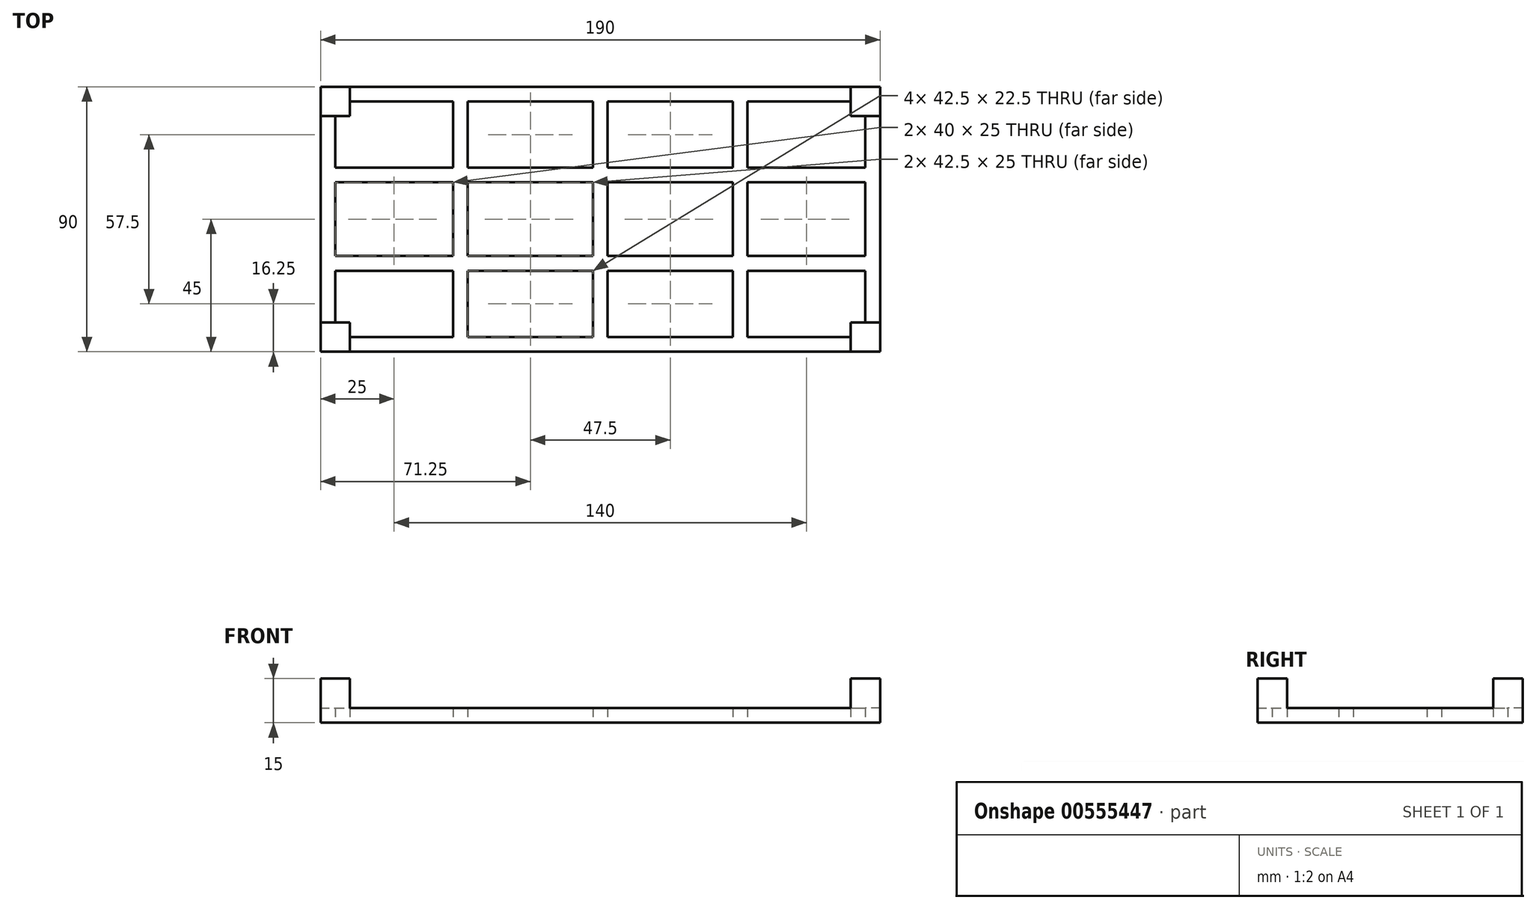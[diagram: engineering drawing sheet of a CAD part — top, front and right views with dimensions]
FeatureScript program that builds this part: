
annotation { "Feature Type Name" : "Feature", "Feature Type Description" : "" }
export const myFeature = defineFeature(function(context is Context, id is Id, definition is map)
    precondition{}
    {
        {
            var Q0;
            Q0=qCreatedBy(makeId("Top.planeOp"),FACE);
            var sketch = newSketch(context, id + "F0", { "sketchPlane" : qUnion([Q0])});
            skLineSegment(sketch, "E0.bottom", {"start": v(0, 0) * mm, "end": v(190, 0) * mm});
            skLineSegment(sketch, "E0.top", {"start": v(0, 90) * mm, "end": v(190, 90) * mm});
            skLineSegment(sketch, "E0.left", {"start": v(0, 0) * mm, "end": v(0, 90) * mm});
            skLineSegment(sketch, "E0.right", {"start": v(190, 0) * mm, "end": v(190, 90) * mm});
            skLineSegment(sketch, "E1", {"start": v(-5.2, 60) * mm, "end": v(194.64, 60) * mm, "construction": true});
            skLineSegment(sketch, "E2", {"start": v(-4.31, 30) * mm, "end": v(194.29, 30) * mm, "construction": true});
            skLineSegment(sketch, "E3", {"start": v(47.5, 94.98) * mm, "end": v(47.5, -5.37) * mm, "construction": true});
            skLineSegment(sketch, "E4", {"start": v(95, 95.69) * mm, "end": v(95, -7.31) * mm, "construction": true});
            skLineSegment(sketch, "E5", {"start": v(142.5, 96.04) * mm, "end": v(142.5, -7.5) * mm, "construction": true});
            skLineSegment(sketch, "E6", {"start": v(45, 85) * mm, "end": v(45, 62.5) * mm});
            skLineSegment(sketch, "E7", {"start": v(92.5, 85) * mm, "end": v(92.5, 62.5) * mm});
            skLineSegment(sketch, "E8", {"start": v(5, 62.5) * mm, "end": v(45, 62.5) * mm});
            skLineSegment(sketch, "E9", {"start": v(5, 57.5) * mm, "end": v(45, 57.5) * mm});
            skLineSegment(sketch, "E10", {"start": v(0, 80) * mm, "end": v(10, 80) * mm});
            skLineSegment(sketch, "E11", {"start": v(10, 90) * mm, "end": v(10, 80) * mm});
            skLineSegment(sketch, "E12", {"start": v(10, 0) * mm, "end": v(10, 10) * mm});
            skLineSegment(sketch, "E13", {"start": v(10, 10) * mm, "end": v(0, 10) * mm});
            skLineSegment(sketch, "E14", {"start": v(190, 10) * mm, "end": v(180, 10) * mm});
            skLineSegment(sketch, "E15", {"start": v(180, 10) * mm, "end": v(180, 0) * mm});
            skLineSegment(sketch, "E16", {"start": v(190, 80) * mm, "end": v(180, 80) * mm});
            skLineSegment(sketch, "E17", {"start": v(180, 80) * mm, "end": v(180, 90) * mm});
            skLineSegment(sketch, "E18.trimOffspring", {"start": v(50, 85) * mm, "end": v(92.5, 85) * mm});
            skLineSegment(sketch, "E19.trimOffspring", {"start": v(10, 85) * mm, "end": v(45, 85) * mm});
            skLineSegment(sketch, "E20.trimOffspring", {"start": v(50, 62.5) * mm, "end": v(92.5, 62.5) * mm});
            skLineSegment(sketch, "E21.trimOffspring", {"start": v(50, 62.5) * mm, "end": v(50, 85) * mm});
            skLineSegment(sketch, "E22.trimOffspring", {"start": v(50, 57.5) * mm, "end": v(92.5, 57.5) * mm});
            skLineSegment(sketch, "E23.trimOffspring", {"start": v(45, 57.5) * mm, "end": v(45, 32.5) * mm});
            skLineSegment(sketch, "E24.trimOffspring", {"start": v(5, 62.5) * mm, "end": v(5, 80) * mm});
            skLineSegment(sketch, "E25.trimOffspring", {"start": v(5, 32.5) * mm, "end": v(5, 57.5) * mm});
            skLineSegment(sketch, "E26.trimOffspring", {"start": v(5, 27.5) * mm, "end": v(45, 27.5) * mm});
            skLineSegment(sketch, "E27.trimOffspring", {"start": v(5, 32.5) * mm, "end": v(45, 32.5) * mm});
            skLineSegment(sketch, "E28.trimOffspring", {"start": v(5, 10) * mm, "end": v(5, 27.5) * mm});
            skLineSegment(sketch, "E29.trimOffspring", {"start": v(10, 5) * mm, "end": v(45, 5) * mm});
            skLineSegment(sketch, "E30.trimOffspring", {"start": v(50, 32.5) * mm, "end": v(92.5, 32.5) * mm});
            skLineSegment(sketch, "E31.trimOffspring", {"start": v(50, 32.5) * mm, "end": v(50, 57.5) * mm});
            skLineSegment(sketch, "E32.trimOffspring", {"start": v(50, 27.5) * mm, "end": v(92.5, 27.5) * mm});
            skLineSegment(sketch, "E33.trimOffspring", {"start": v(45, 27.5) * mm, "end": v(45, 5) * mm});
            skLineSegment(sketch, "E34.trimOffspring", {"start": v(92.5, 27.5) * mm, "end": v(92.5, 5) * mm});
            skLineSegment(sketch, "E35.trimOffspring", {"start": v(97.5, 27.5) * mm, "end": v(140, 27.5) * mm});
            skLineSegment(sketch, "E36.trimOffspring", {"start": v(97.5, 32.5) * mm, "end": v(97.5, 57.5) * mm});
            skLineSegment(sketch, "E37.trimOffspring", {"start": v(97.5, 32.5) * mm, "end": v(140, 32.5) * mm});
            skLineSegment(sketch, "E38.trimOffspring", {"start": v(97.5, 57.5) * mm, "end": v(140, 57.5) * mm});
            skLineSegment(sketch, "E39.trimOffspring", {"start": v(97.5, 62.5) * mm, "end": v(97.5, 85) * mm});
            skLineSegment(sketch, "E40.trimOffspring", {"start": v(97.5, 62.5) * mm, "end": v(140, 62.5) * mm});
            skLineSegment(sketch, "E41.trimOffspring", {"start": v(92.5, 57.5) * mm, "end": v(92.5, 32.5) * mm});
            skLineSegment(sketch, "E42.trimOffspring", {"start": v(50, 5) * mm, "end": v(92.5, 5) * mm});
            skLineSegment(sketch, "E43.trimOffspring", {"start": v(50, 5) * mm, "end": v(50, 27.5) * mm});
            skLineSegment(sketch, "E44.trimOffspring", {"start": v(97.5, 5) * mm, "end": v(140, 5) * mm});
            skLineSegment(sketch, "E45.trimOffspring", {"start": v(97.5, 5) * mm, "end": v(97.5, 27.5) * mm});
            skLineSegment(sketch, "E46.trimOffspring", {"start": v(97.5, 85) * mm, "end": v(140, 85) * mm});
            skLineSegment(sketch, "E47.trimOffspring", {"start": v(140, 85) * mm, "end": v(140, 62.5) * mm});
            skLineSegment(sketch, "E48.trimOffspring", {"start": v(145, 85) * mm, "end": v(180, 85) * mm});
            skLineSegment(sketch, "E49.trimOffspring", {"start": v(145, 62.5) * mm, "end": v(185, 62.5) * mm});
            skLineSegment(sketch, "E50.trimOffspring", {"start": v(140, 57.5) * mm, "end": v(140, 32.5) * mm});
            skLineSegment(sketch, "E51.trimOffspring", {"start": v(145, 57.5) * mm, "end": v(185, 57.5) * mm});
            skLineSegment(sketch, "E52.trimOffspring", {"start": v(145, 62.5) * mm, "end": v(145, 85) * mm});
            skLineSegment(sketch, "E53.trimOffspring", {"start": v(145, 32.5) * mm, "end": v(185, 32.5) * mm});
            skLineSegment(sketch, "E54.trimOffspring", {"start": v(145, 27.5) * mm, "end": v(185, 27.5) * mm});
            skLineSegment(sketch, "E55.trimOffspring", {"start": v(145, 32.5) * mm, "end": v(145, 57.5) * mm});
            skLineSegment(sketch, "E56.trimOffspring", {"start": v(140, 27.5) * mm, "end": v(140, 5) * mm});
            skLineSegment(sketch, "E57.trimOffspring", {"start": v(145, 5) * mm, "end": v(180, 5) * mm});
            skLineSegment(sketch, "E58.trimOffspring", {"start": v(145, 5) * mm, "end": v(145, 27.5) * mm});
            skLineSegment(sketch, "E59.trimOffspring", {"start": v(185, 10) * mm, "end": v(185, 27.5) * mm});
            skLineSegment(sketch, "E60.trimOffspring", {"start": v(185, 32.5) * mm, "end": v(185, 57.5) * mm});
            skLineSegment(sketch, "E61.trimOffspring", {"start": v(185, 62.5) * mm, "end": v(185, 80) * mm});
            skSolve(sketch);
        }
        {
            var Q0;
            Q0=makeQuery(id+"F0.imprint","IMPRINT",FACE,{"disambiguationData":[TD([[makeQuery(id+"F0.imprint","IMPRINT",EDGE,{"derivedFrom":sQuery(id+"F0.wireOp",EDGE,"E6")}),1.0]])]});
            var Q1;
            {var subQ4=sQuery(id+"F0.wireOp",EDGE,"E0.left");var subQ6=sQuery(id+"F0.wireOp",EDGE,"E0.top");var subQ7=makeQuery(id+"F0.imprint","INTERSECT",VERTEX,{"derivedFrom":[subQ6,subQ4]});Q1=makeQuery(id+"F0.imprint","IMPRINT",FACE,{"disambiguationData":[TD([[makeQuery(id+"F0.imprint","IMPRINT",EDGE,{"disambiguationData":[TD([[subQ7,-1.0]])],"derivedFrom":subQ6}),-1.0]])]});}
            var Q2;
            {var subQ4=sQuery(id+"F0.wireOp",EDGE,"E0.left");var subQ5=sQuery(id+"F0.wireOp",EDGE,"E0.bottom");var subQ6=makeQuery(id+"F0.imprint","INTERSECT",VERTEX,{"derivedFrom":[subQ5,subQ4]});Q2=makeQuery(id+"F0.imprint","IMPRINT",FACE,{"disambiguationData":[TD([[makeQuery(id+"F0.imprint","IMPRINT",EDGE,{"disambiguationData":[TD([[subQ6,-1.0]])],"derivedFrom":subQ5}),1.0]])]});}
            var Q3;
            {var subQ4=sQuery(id+"F0.wireOp",EDGE,"E0.right");var subQ6=sQuery(id+"F0.wireOp",EDGE,"E0.top");var subQ7=makeQuery(id+"F0.imprint","INTERSECT",VERTEX,{"derivedFrom":[subQ6,subQ4]});Q3=makeQuery(id+"F0.imprint","IMPRINT",FACE,{"disambiguationData":[TD([[makeQuery(id+"F0.imprint","IMPRINT",EDGE,{"disambiguationData":[TD([[subQ7,1.0]])],"derivedFrom":subQ6}),-1.0]])]});}
            var Q4;
            {var subQ4=sQuery(id+"F0.wireOp",EDGE,"E0.right");var subQ6=sQuery(id+"F0.wireOp",EDGE,"E0.bottom");var subQ7=makeQuery(id+"F0.imprint","INTERSECT",VERTEX,{"derivedFrom":[subQ6,subQ4]});Q4=makeQuery(id+"F0.imprint","IMPRINT",FACE,{"disambiguationData":[TD([[makeQuery(id+"F0.imprint","IMPRINT",EDGE,{"disambiguationData":[TD([[subQ7,1.0]])],"derivedFrom":subQ6}),1.0]])]});}
            extrude(context, id + "F1", {"entities" : qUnion([Q0, Q1, Q2, Q3, Q4]), "depth" : 5 * mm, "offsetDistance" : 25 * mm});
        }
        {
            var Q0;
            Q0=makeQuery(id+"F1.opExtrude","CAP_FACE",FACE,{"disambiguationData":[OSD([sQuery(id+"F0.wireOp",EDGE,"E0.bottom"),sQuery(id+"F0.wireOp",EDGE,"E0.top"),sQuery(id+"F0.wireOp",EDGE,"E0.left"),sQuery(id+"F0.wireOp",EDGE,"E0.right"),sQuery(id+"F0.wireOp",EDGE,"E6"),sQuery(id+"F0.wireOp",EDGE,"E7"),sQuery(id+"F0.wireOp",EDGE,"E8"),sQuery(id+"F0.wireOp",EDGE,"E9"),sQuery(id+"F0.wireOp",EDGE,"E10"),sQuery(id+"F0.wireOp",EDGE,"E11"),sQuery(id+"F0.wireOp",EDGE,"E12"),sQuery(id+"F0.wireOp",EDGE,"E13"),sQuery(id+"F0.wireOp",EDGE,"E14"),sQuery(id+"F0.wireOp",EDGE,"E15"),sQuery(id+"F0.wireOp",EDGE,"E16"),sQuery(id+"F0.wireOp",EDGE,"E17"),sQuery(id+"F0.wireOp",EDGE,"E18.trimOffspring"),sQuery(id+"F0.wireOp",EDGE,"E19.trimOffspring"),sQuery(id+"F0.wireOp",EDGE,"E20.trimOffspring"),sQuery(id+"F0.wireOp",EDGE,"E21.trimOffspring"),sQuery(id+"F0.wireOp",EDGE,"E22.trimOffspring"),sQuery(id+"F0.wireOp",EDGE,"E23.trimOffspring"),sQuery(id+"F0.wireOp",EDGE,"E24.trimOffspring"),sQuery(id+"F0.wireOp",EDGE,"E25.trimOffspring"),sQuery(id+"F0.wireOp",EDGE,"E26.trimOffspring"),sQuery(id+"F0.wireOp",EDGE,"E27.trimOffspring"),sQuery(id+"F0.wireOp",EDGE,"E28.trimOffspring"),sQuery(id+"F0.wireOp",EDGE,"E29.trimOffspring"),sQuery(id+"F0.wireOp",EDGE,"E30.trimOffspring"),sQuery(id+"F0.wireOp",EDGE,"E31.trimOffspring"),sQuery(id+"F0.wireOp",EDGE,"E32.trimOffspring"),sQuery(id+"F0.wireOp",EDGE,"E33.trimOffspring"),sQuery(id+"F0.wireOp",EDGE,"E34.trimOffspring"),sQuery(id+"F0.wireOp",EDGE,"E35.trimOffspring"),sQuery(id+"F0.wireOp",EDGE,"E36.trimOffspring"),sQuery(id+"F0.wireOp",EDGE,"E37.trimOffspring"),sQuery(id+"F0.wireOp",EDGE,"E38.trimOffspring"),sQuery(id+"F0.wireOp",EDGE,"E39.trimOffspring"),sQuery(id+"F0.wireOp",EDGE,"E40.trimOffspring"),sQuery(id+"F0.wireOp",EDGE,"E41.trimOffspring"),sQuery(id+"F0.wireOp",EDGE,"E42.trimOffspring"),sQuery(id+"F0.wireOp",EDGE,"E43.trimOffspring"),sQuery(id+"F0.wireOp",EDGE,"E44.trimOffspring"),sQuery(id+"F0.wireOp",EDGE,"E45.trimOffspring"),sQuery(id+"F0.wireOp",EDGE,"E46.trimOffspring"),sQuery(id+"F0.wireOp",EDGE,"E47.trimOffspring"),sQuery(id+"F0.wireOp",EDGE,"E48.trimOffspring"),sQuery(id+"F0.wireOp",EDGE,"E49.trimOffspring"),sQuery(id+"F0.wireOp",EDGE,"E50.trimOffspring"),sQuery(id+"F0.wireOp",EDGE,"E51.trimOffspring"),sQuery(id+"F0.wireOp",EDGE,"E52.trimOffspring"),sQuery(id+"F0.wireOp",EDGE,"E53.trimOffspring"),sQuery(id+"F0.wireOp",EDGE,"E54.trimOffspring"),sQuery(id+"F0.wireOp",EDGE,"E55.trimOffspring"),sQuery(id+"F0.wireOp",EDGE,"E56.trimOffspring"),sQuery(id+"F0.wireOp",EDGE,"E57.trimOffspring"),sQuery(id+"F0.wireOp",EDGE,"E58.trimOffspring"),sQuery(id+"F0.wireOp",EDGE,"E59.trimOffspring"),sQuery(id+"F0.wireOp",EDGE,"E60.trimOffspring"),sQuery(id+"F0.wireOp",EDGE,"E61.trimOffspring")])],"isStart":false});
            var sketch = newSketch(context, id + "F2", { "sketchPlane" : qUnion([Q0])});
            skLineSegment(sketch, "E62.bottom", {"start": v(0, 90) * mm, "end": v(10, 90) * mm});
            skLineSegment(sketch, "E62.top", {"start": v(0, 80) * mm, "end": v(10, 80) * mm});
            skLineSegment(sketch, "E62.left", {"start": v(0, 90) * mm, "end": v(0, 80) * mm});
            skLineSegment(sketch, "E62.right", {"start": v(10, 90) * mm, "end": v(10, 80) * mm});
            skLineSegment(sketch, "E63.bottom", {"start": v(190, 90) * mm, "end": v(180, 90) * mm});
            skLineSegment(sketch, "E63.top", {"start": v(190, 80) * mm, "end": v(180, 80) * mm});
            skLineSegment(sketch, "E63.left", {"start": v(190, 90) * mm, "end": v(190, 80) * mm});
            skLineSegment(sketch, "E63.right", {"start": v(180, 90) * mm, "end": v(180, 80) * mm});
            skLineSegment(sketch, "E64.bottom", {"start": v(190, 0) * mm, "end": v(180, 0) * mm});
            skLineSegment(sketch, "E64.top", {"start": v(190, 10) * mm, "end": v(180, 10) * mm});
            skLineSegment(sketch, "E64.left", {"start": v(190, 0) * mm, "end": v(190, 10) * mm});
            skLineSegment(sketch, "E64.right", {"start": v(180, 0) * mm, "end": v(180, 10) * mm});
            skLineSegment(sketch, "E65.bottom", {"start": v(0, 0) * mm, "end": v(10, 0) * mm});
            skLineSegment(sketch, "E65.top", {"start": v(0, 10) * mm, "end": v(10, 10) * mm});
            skLineSegment(sketch, "E65.left", {"start": v(0, 0) * mm, "end": v(0, 10) * mm});
            skLineSegment(sketch, "E65.right", {"start": v(10, 0) * mm, "end": v(10, 10) * mm});
            skSolve(sketch);
        }
        {
            var Q0;
            {var subQ5=sQuery(id+"F2.wireOp",EDGE,"E62.bottom");Q0=makeQuery(id+"F2.imprint","IMPRINT",FACE,{"disambiguationData":[TD([[makeQuery(id+"F2.imprint","IMPRINT",EDGE,{"derivedFrom":subQ5}),-1.0]])]});}
            var Q1;
            {var subQ5=sQuery(id+"F2.wireOp",EDGE,"E63.bottom");Q1=makeQuery(id+"F2.imprint","IMPRINT",FACE,{"disambiguationData":[TD([[makeQuery(id+"F2.imprint","IMPRINT",EDGE,{"derivedFrom":subQ5}),-1.0]])]});}
            var Q2;
            {var subQ5=sQuery(id+"F2.wireOp",EDGE,"E64.bottom");Q2=makeQuery(id+"F2.imprint","IMPRINT",FACE,{"disambiguationData":[TD([[makeQuery(id+"F2.imprint","IMPRINT",EDGE,{"derivedFrom":subQ5}),1.0]])]});}
            var Q3;
            {var subQ5=sQuery(id+"F2.wireOp",EDGE,"E65.bottom");Q3=makeQuery(id+"F2.imprint","IMPRINT",FACE,{"disambiguationData":[TD([[makeQuery(id+"F2.imprint","IMPRINT",EDGE,{"derivedFrom":subQ5}),1.0]])]});}
            extrude(context, id + "F3", {"entities" : qUnion([Q0, Q1, Q2, Q3]), "operationType" : NewBodyOperationType.ADD, "depth" : 10 * mm, "offsetDistance" : 25 * mm});
        }
    });
